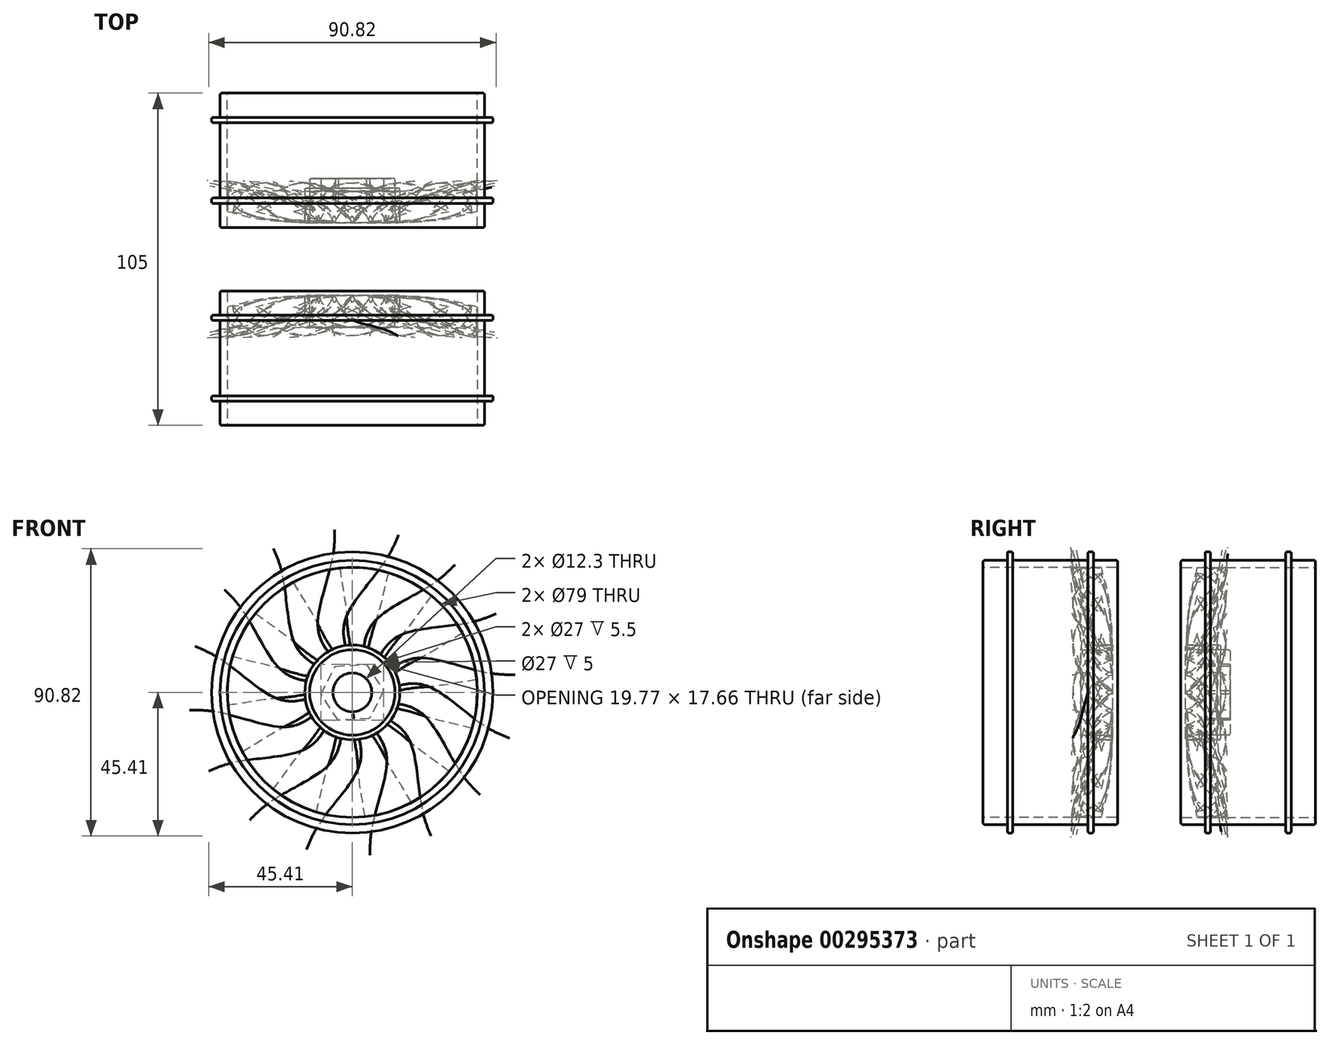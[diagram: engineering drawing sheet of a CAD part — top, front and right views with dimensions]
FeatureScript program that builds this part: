
annotation { "Feature Type Name" : "Feature", "Feature Type Description" : "" }
export const myFeature = defineFeature(function(context is Context, id is Id, definition is map)
    precondition{}
    {
        {
            var Q0;
            Q0=qCreatedBy(makeId("Front.planeOp"),FACE);
            var sketch = newSketch(context, id + "F0", { "sketchPlane" : qUnion([Q0])});
            skCircle(sketch, "E0", {"center": v(0, 0) * mm, "radius": 41.75 * mm});
            skCircle(sketch, "E1", {"center": v(0, 0) * mm, "radius": 55 * mm, "construction": true});
            skCircle(sketch, "E2", {"center": v(0, 0) * mm, "radius": 6.15 * mm});
            skCircle(sketch, "E3", {"center": v(0, 0) * mm, "radius": 39.5 * mm});
            skCircle(sketch, "E4", {"center": v(0, 0) * mm, "radius": 13.5 * mm});
            skCircle(sketch, "E5", {"center": v(0, 0) * mm, "radius": 15 * mm});
            skCircle(sketch, "E6.cCircle", {"center": v(0, 0) * mm, "radius": 9.9 * mm, "construction": true});
            skLineSegment(sketch, "E6.0", {"start": v(9.89, 0.54) * mm, "end": v(5.41, -8.3) * mm});
            skLineSegment(sketch, "E6.1", {"start": v(5.41, -8.3) * mm, "end": v(-4.47, -8.83) * mm});
            skLineSegment(sketch, "E6.2", {"start": v(-4.47, -8.83) * mm, "end": v(-9.89, -0.54) * mm});
            skLineSegment(sketch, "E6.3", {"start": v(-9.89, -0.54) * mm, "end": v(-5.41, 8.3) * mm});
            skLineSegment(sketch, "E6.4", {"start": v(-5.41, 8.3) * mm, "end": v(4.47, 8.83) * mm});
            skLineSegment(sketch, "E6.5", {"start": v(4.47, 8.83) * mm, "end": v(9.89, 0.54) * mm});
            skSolve(sketch);
        }
        {
            var Q0;
            Q0=makeQuery(id+"F0.imprint","IMPRINT",FACE,{"disambiguationData":[TD([[makeQuery(id+"F0.imprint","IMPRINT",EDGE,{"derivedFrom":sQuery(id+"F0.wireOp",EDGE,"E0")}),1.0]])]});
            extrude(context, id + "F1", {"entities" : qUnion([Q0]), "depth" : 3.5 * mm, "hasSecondDirection" : true, "secondDirectionOppositeDirection" : true, "secondDirectionDepth" : 39 * mm});
        }
        {
            var Q0;
            Q0=makeQuery(id+"F1.opExtrude","CAP_EDGE",EDGE,{"disambiguationData":[OSD([sQuery(id+"F0.wireOp",EDGE,"E3")])],"isStart":false});
            var Q1;
            Q1=makeQuery(id+"F1.opExtrude","CAP_EDGE",EDGE,{"disambiguationData":[OSD([sQuery(id+"F0.wireOp",EDGE,"E0")])],"isStart":false});
            var Q2;
            Q2=makeQuery(id+"F1.opExtrude","CAP_EDGE",EDGE,{"disambiguationData":[OSD([sQuery(id+"F0.wireOp",EDGE,"E3")])],"isStart":true});
            var Q3;
            Q3=makeQuery(id+"F1.opExtrude","CAP_EDGE",EDGE,{"disambiguationData":[OSD([sQuery(id+"F0.wireOp",EDGE,"E0")])],"isStart":true});
            fillet(context, id + "F2", {"entities" : qUnion([Q0, Q1, Q2, Q3]), "radius" : .5 * mm, "tangentPropagation" : true, "allowEdgeOverflow" : false});
        }
        {
            var Q0;
            Q0=makeQuery(id+"F0.imprint","IMPRINT",FACE,{"disambiguationData":[TD([[makeQuery(id+"F0.imprint","IMPRINT",EDGE,{"derivedFrom":sQuery(id+"F0.wireOp",EDGE,"E4")}),-1.0]])]});
            extrude(context, id + "F3", {"entities" : qUnion([Q0]), "oppositeDirection" : true, "depth" : 4 * mm, "hasSecondDirection" : true, "secondDirectionOppositeDirection" : false, "secondDirectionDepth" : 2 * mm, "offsetDistance" : 25 * mm});
        }
        {
            var Q0;
            Q0=makeQuery(id+"F0.imprint","IMPRINT",FACE,{"disambiguationData":[TD([[makeQuery(id+"F0.imprint","IMPRINT",EDGE,{"derivedFrom":sQuery(id+"F0.wireOp",EDGE,"E4")}),1.0]])]});
            var Q1;
            Q1=makeQuery(id+"F0.imprint","IMPRINT",FACE,{"disambiguationData":[TD([[makeQuery(id+"F0.imprint","IMPRINT",EDGE,{"derivedFrom":sQuery(id+"F0.wireOp",EDGE,"E2")}),-1.0]])]});
            extrude(context, id + "F4", {"entities" : qUnion([Q0, Q1]), "operationType" : NewBodyOperationType.ADD, "oppositeDirection" : true, "depth" : 8 * mm, "offsetDistance" : 25 * mm});
        }
        {
            var Q0;
            Q0=qCreatedBy(makeId("Top.planeOp"),FACE);
            cPlane(context, id + "F5", {"entities" : qUnion([Q0]), "cplaneType" : CPlaneType.OFFSET, "offset" : 12 * mm, "width" : 150 * mm, "height" : 150 * mm});
        }
        {
            var Q0;
            Q0=qCreatedBy(id+"F5.planeOp",FACE);
            var sketch = newSketch(context, id + "F6", { "sketchPlane" : qUnion([Q0])});
            skFitSpline(sketch, "E7", {"points": [v(0.53, -1.24) * mm, v(0.2, -1.6) * mm, v(-0.52, -1.05) * mm, v(-0.35, 1.79) * mm, v(0.58, 3.7) * mm, v(-0.1, -0.17) * mm, v(0.53, -1.24) * mm]});
            skSolve(sketch);
        }
        {
            var Q0;
            Q0=qCreatedBy(makeId("Top.planeOp"),FACE);
            cPlane(context, id + "F7", {"entities" : qUnion([Q0]), "cplaneType" : CPlaneType.OFFSET, "offset" : 40 * mm, "width" : 150 * mm, "height" : 150 * mm});
        }
        {
            var Q0;
            Q0=qCreatedBy(id+"F7.planeOp",FACE);
            var sketch = newSketch(context, id + "F8", { "sketchPlane" : qUnion([Q0])});
            skFitSpline(sketch, "E8", {"points": [v(-2.34, 1.57) * mm, v(-4.55, -0.94) * mm, v(-2.86, 4.8) * mm, v(9.88, 20.61) * mm, v(20.44, 27.72) * mm, v(5.15, 13.05) * mm, v(-2.34, 1.57) * mm]});
            skSolve(sketch);
        }
        {
            var Q0;
            Q0=qCreatedBy(id+"F5.planeOp",FACE);
            cPlane(context, id + "F9", {"entities" : qUnion([Q0]), "cplaneType" : CPlaneType.OFFSET, "offset" : 22 * mm, "width" : 150 * mm, "height" : 150 * mm});
        }
        {
            var Q0;
            Q0=qCreatedBy(id+"F9.planeOp",FACE);
            var sketch = newSketch(context, id + "F10", { "sketchPlane" : qUnion([Q0])});
            skPoint(sketch, "E9", {"position": v(-3.45, -1.13) * mm});
            skPoint(sketch, "E10", {"position": v(15.69, 22.06) * mm});
            skFitSpline(sketch, "E11", {"points": [v(-3.45, -1.13) * mm, v(-3.45, 2.76) * mm, v(4.28, 15.4) * mm, v(15.69, 22.06) * mm, v(4.3, 11.2) * mm, v(0, 0.78) * mm, v(-3.45, -1.13) * mm]});
            skSolve(sketch);
        }
        {
            var Q0;
            Q0=qCreatedBy(id+"F5.planeOp",FACE);
            cPlane(context, id + "F11", {"entities" : qUnion([Q0]), "cplaneType" : CPlaneType.OFFSET, "offset" : 10 * mm, "width" : 150 * mm, "height" : 150 * mm});
        }
        {
            var Q0;
            Q0=qCreatedBy(id+"F11.planeOp",FACE);
            var sketch = newSketch(context, id + "F12", { "sketchPlane" : qUnion([Q0])});
            skPoint(sketch, "E12", {"position": v(-1.84, -1.52) * mm});
            skFitSpline(sketch, "E13", {"points": [v(-1.84, -1.52) * mm, v(-1.84, 0.36) * mm, v(0.33, 5.91) * mm, v(2.1, 7.53) * mm, v(0.53, 2.14) * mm, v(-0.13, -1.72) * mm, v(-1.84, -1.52) * mm]});
            skSolve(sketch);
        }
        {
            var Q0;
            Q0=makeQuery(id+"F6.imprint","IMPRINT",FACE,{"disambiguationData":[TD([[makeQuery(id+"F6.imprint","IMPRINT",EDGE,{"derivedFrom":sQuery(id+"F6.wireOp",EDGE,"E7")}),-1.0]])]});
            var Q1;
            Q1=makeQuery(id+"F12.imprint","IMPRINT",FACE,{"disambiguationData":[TD([[makeQuery(id+"F12.imprint","IMPRINT",EDGE,{"derivedFrom":sQuery(id+"F12.wireOp",EDGE,"E13")}),-1.0]])]});
            var Q2;
            Q2=makeQuery(id+"F10.imprint","IMPRINT",FACE,{"disambiguationData":[TD([[makeQuery(id+"F10.imprint","IMPRINT",EDGE,{"derivedFrom":sQuery(id+"F10.wireOp",EDGE,"E11")}),-1.0]])]});
            var Q3;
            Q3=makeQuery(id+"F8.imprint","IMPRINT",FACE,{"disambiguationData":[TD([[makeQuery(id+"F8.imprint","IMPRINT",EDGE,{"derivedFrom":sQuery(id+"F8.wireOp",EDGE,"E8")}),-1.0]])]});
            var Q4;
            Q4=sQuery(id+"F12.wireOp",VERTEX,"E12");
            var Q5;
            Q5=sQuery(id+"F6.wireOp",VERTEX,"E7.1.internal");
            var Q6;
            Q6=sQuery(id+"F10.wireOp",VERTEX,"E9");
            var Q7;
            Q7=sQuery(id+"F8.wireOp",VERTEX,"E8.1.internal");
            loft(context, id + "F13", {"sheetProfilesArray" : [{ "sheetProfileEntities" : qUnion([Q0]) }, { "sheetProfileEntities" : qUnion([Q1]) }, { "sheetProfileEntities" : qUnion([Q2]) }, { "sheetProfileEntities" : qUnion([Q3]) }], "connections" : [{ "connectionEntities" : qUnion([Q4, Q5, Q6, Q7]), "connectionEdgeQueries" : qUnion([]), "connectionEdgeParameters" : [] }]});
        }
        {
            var Q0;
            Q0=qCreatedBy(makeId("Right.planeOp"),FACE);
            var sketch = newSketch(context, id + "F14", { "sketchPlane" : qUnion([Q0])});
            skLineSegment(sketch, "E14", {"start": v(-1.68, 13.92) * mm, "end": v(0, 48.42) * mm});
            skSolve(sketch);
        }
        {
            var Q0;
            Q0=makeQuery(id+"F13.opLoft","SWEPT_BODY",BODY,{"disambiguationData":[OSD([makeQuery(id+"F6.imprint","IMPRINT",FACE,{"disambiguationData":[TD([[makeQuery(id+"F6.imprint","IMPRINT",EDGE,{"derivedFrom":sQuery(id+"F6.wireOp",EDGE,"E7")}),-1.0]])]}),makeQuery(id+"F8.imprint","IMPRINT",FACE,{"disambiguationData":[TD([[makeQuery(id+"F8.imprint","IMPRINT",EDGE,{"derivedFrom":sQuery(id+"F8.wireOp",EDGE,"E8")}),-1.0]])]}),sQuery(id+"F10.wireOp",EDGE,"E11"),sQuery(id+"F12.wireOp",EDGE,"E13")])]});
            var Q1;
            Q1=sQuery(id+"F14.wireOp",EDGE,"E14");
            transform(context, id + "F15", {"entities" : qUnion([Q0]), "transformType" : TransformType.ROTATION, "transformAxis" : qUnion([Q1]), "angle" : 35 * degree, "oppositeDirection" : true, "makeCopy" : false});
        }
        {
            var Q0;
            Q0=makeQuery(id+"F1.opExtrude","SWEPT_BODY",BODY,{"disambiguationData":[OSD([sQuery(id+"F0.wireOp",EDGE,"E0"),sQuery(id+"F0.wireOp",EDGE,"E3")])]});
            var Q1;
            Q1=makeQuery(id+"F13.opLoft","SWEPT_BODY",BODY,{"disambiguationData":[OSD([makeQuery(id+"F6.imprint","IMPRINT",FACE,{"disambiguationData":[TD([[makeQuery(id+"F6.imprint","IMPRINT",EDGE,{"derivedFrom":sQuery(id+"F6.wireOp",EDGE,"E7")}),-1.0]])]}),makeQuery(id+"F8.imprint","IMPRINT",FACE,{"disambiguationData":[TD([[makeQuery(id+"F8.imprint","IMPRINT",EDGE,{"derivedFrom":sQuery(id+"F8.wireOp",EDGE,"E8")}),-1.0]])]}),sQuery(id+"F10.wireOp",EDGE,"E11"),sQuery(id+"F12.wireOp",EDGE,"E13")])]});
            var Q2;
            Q2=makeQuery(id+"F1.opExtrude","SWEPT_FACE",FACE,{"disambiguationData":[OSD([sQuery(id+"F0.wireOp",EDGE,"E0")])]});
            booleanBodies(context, id + "F16", {"operationType" : BooleanOperationType.SUBTRACTION, "tools" : qUnion([Q0]), "targets" : qUnion([Q1]), "offset" : true, "entitiesToOffset" : qUnion([Q2]), "offsetDistance" : 15 * mm, "keepTools" : true});
        }
        {
            var Q0;
            Q0=makeQuery(id+"F21.boolean.opBoolean","SPLIT",BODY,{"disambiguationData":[OD(0.0)],"derivedFrom":makeQuery(id+"F3.opExtrude","SWEPT_BODY",BODY,{"disambiguationData":[OSD([sQuery(id+"F0.wireOp",EDGE,"E4"),sQuery(id+"F0.wireOp",EDGE,"E5")])]})});
            var Q1;
            Q1=makeQuery(id+"F13.opLoft","SWEPT_BODY",BODY,{"disambiguationData":[OSD([makeQuery(id+"F6.imprint","IMPRINT",FACE,{"disambiguationData":[TD([[makeQuery(id+"F6.imprint","IMPRINT",EDGE,{"derivedFrom":sQuery(id+"F6.wireOp",EDGE,"E7")}),-1.0]])]}),makeQuery(id+"F8.imprint","IMPRINT",FACE,{"disambiguationData":[TD([[makeQuery(id+"F8.imprint","IMPRINT",EDGE,{"derivedFrom":sQuery(id+"F8.wireOp",EDGE,"E8")}),-1.0]])]}),sQuery(id+"F10.wireOp",EDGE,"E11"),sQuery(id+"F12.wireOp",EDGE,"E13")])]});
            var Q2;
            {var subQ0=sQuery(id+"F0.wireOp",EDGE,"E4");Q2=makeQuery(id+"F21.boolean.opBoolean","MERGE",FACE,{"derivedFrom":[makeQuery(id+"F3.opExtrude","SWEPT_FACE",FACE,{"disambiguationData":[OSD([subQ0])]}),makeQuery(id+"F21.opExtrude","SWEPT_FACE",FACE,{"disambiguationData":[OSD([subQ0])]})]});}
            var Q3;
            {var subQ0=sQuery(id+"F0.wireOp",EDGE,"E4");Q3=makeQuery(id+"F29.opFillet","BLEND_FACE",FACE,{"disambiguationData":[OSD([subQ0]),TDD([makeQuery(id+"F3.opExtrude","CAP_EDGE",EDGE,{"disambiguationData":[OSD([subQ0])],"isStart":true})])]});}
            booleanBodies(context, id + "F17", {"operationType" : BooleanOperationType.SUBTRACTION, "tools" : qUnion([Q0]), "targets" : qUnion([Q1]), "offset" : true, "entitiesToOffset" : qUnion([Q2, Q3]), "offsetDistance" : 5 * mm, "keepTools" : true});
        }
        {
            var Q0;
            Q0=makeQuery(id+"F13.opLoft","SWEPT_BODY",BODY,{"disambiguationData":[OSD([makeQuery(id+"F6.imprint","IMPRINT",FACE,{"disambiguationData":[TD([[makeQuery(id+"F6.imprint","IMPRINT",EDGE,{"derivedFrom":sQuery(id+"F6.wireOp",EDGE,"E7")}),-1.0]])]}),makeQuery(id+"F8.imprint","IMPRINT",FACE,{"disambiguationData":[TD([[makeQuery(id+"F8.imprint","IMPRINT",EDGE,{"derivedFrom":sQuery(id+"F8.wireOp",EDGE,"E8")}),-1.0]])]}),sQuery(id+"F10.wireOp",EDGE,"E11"),sQuery(id+"F12.wireOp",EDGE,"E13")])]});
            var Q1;
            Q1=makeQuery(id+"F4.opExtrude","SWEPT_FACE",FACE,{"disambiguationData":[OSD([sQuery(id+"F0.wireOp",EDGE,"E2")])]});
            circularPattern(context, id + "F18", {"entities" : qUnion([Q0]), "axis" : qUnion([Q1]), "angle" : 360 * degree, "instanceCount" : 16, "equalSpace" : true});
        }
        {
            var Q0;
            {var subQ0=sQuery(id+"F0.wireOp",EDGE,"E4");Q0=makeQuery(id+"F4.boolean.opBoolean","MERGE",FACE,{"derivedFrom":[makeQuery(id+"F3.opExtrude","CAP_FACE",FACE,{"disambiguationData":[OSD([subQ0,sQuery(id+"F0.wireOp",EDGE,"E5")])],"isStart":false}),makeQuery(id+"F4.opExtrude","CAP_FACE",FACE,{"disambiguationData":[OSD([sQuery(id+"F0.wireOp",EDGE,"E2"),subQ0])],"isStart":false})]});}
            var sketch = newSketch(context, id + "F19", { "sketchPlane" : qUnion([Q0])});
            skLineSegment(sketch, "E15.0", {"start": v(9.89, -0.54) * mm, "end": v(5.41, 8.3) * mm});
            skLineSegment(sketch, "E15.1", {"start": v(5.41, 8.3) * mm, "end": v(-4.47, 8.83) * mm});
            skLineSegment(sketch, "E15.2", {"start": v(-4.47, 8.83) * mm, "end": v(-9.89, 0.54) * mm});
            skLineSegment(sketch, "E15.3", {"start": v(-9.89, 0.54) * mm, "end": v(-5.41, -8.3) * mm});
            skLineSegment(sketch, "E15.4", {"start": v(-5.41, -8.3) * mm, "end": v(4.47, -8.83) * mm});
            skLineSegment(sketch, "E15.5", {"start": v(4.47, -8.83) * mm, "end": v(9.89, -0.54) * mm});
            skSolve(sketch);
        }
        {
            var Q0;
            Q0=makeQuery(id+"F19.imprint","IMPRINT",FACE,{"disambiguationData":[TD([[makeQuery(id+"F19.imprint","IMPRINT",EDGE,{"derivedFrom":sQuery(id+"F19.wireOp",EDGE,"E15.0")}),-1.0]])]});
            extrude(context, id + "F20", {"entities" : qUnion([Q0]), "depth" : 8 * mm, "offsetDistance" : 25 * mm});
        }
        {
            var Q0;
            Q0=makeQuery(id+"F4.opExtrude","CAP_FACE",FACE,{"disambiguationData":[OSD([sQuery(id+"F0.wireOp",EDGE,"E2"),sQuery(id+"F0.wireOp",EDGE,"E4")])],"isStart":true});
            extrude(context, id + "F21", {"entities" : qUnion([Q0]), "operationType" : NewBodyOperationType.REMOVE, "oppositeDirection" : true, "depth" : 4 * mm, "offsetDistance" : 25 * mm});
        }
        {
            var Q0;
            Q0=makeQuery(id+"F1.opExtrude","CAP_FACE",FACE,{"disambiguationData":[OSD([sQuery(id+"F0.wireOp",EDGE,"E0"),sQuery(id+"F0.wireOp",EDGE,"E3")])],"isStart":false});
            cPlane(context, id + "F22", {"entities" : qUnion([Q0]), "cplaneType" : CPlaneType.OFFSET, "offset" : 8.5 * mm, "oppositeDirection" : true, "width" : 150 * mm, "height" : 150 * mm});
        }
        {
            var Q0;
            Q0=qCreatedBy(id+"F22.planeOp",FACE);
            var sketch = newSketch(context, id + "F23", { "sketchPlane" : qUnion([Q0])});
            skCircle(sketch, "E16", {"center": v(0, 0) * mm, "radius": 44.45 * mm});
            skCircle(sketch, "E17", {"center": v(0, 0) * mm, "radius": 41.75 * mm});
            skSolve(sketch);
        }
        {
            var Q0;
            Q0=makeQuery(id+"F23.imprint","IMPRINT",FACE,{"disambiguationData":[TD([[makeQuery(id+"F23.imprint","IMPRINT",EDGE,{"derivedFrom":sQuery(id+"F23.wireOp",EDGE,"E16")}),1.0]])]});
            extrude(context, id + "F24", {"entities" : qUnion([Q0]), "operationType" : NewBodyOperationType.ADD, "depth" : 1.7 * mm, "offsetDistance" : 25 * mm, "symmetric" : true});
        }
        {
            var Q0;
            Q0=makeQuery(id+"F1.opExtrude","CAP_FACE",FACE,{"disambiguationData":[OSD([sQuery(id+"F0.wireOp",EDGE,"E0"),sQuery(id+"F0.wireOp",EDGE,"E3")])],"isStart":false});
            cPlane(context, id + "F25", {"entities" : qUnion([Q0]), "cplaneType" : CPlaneType.OFFSET, "offset" : 34 * mm, "oppositeDirection" : true, "width" : 150 * mm, "height" : 150 * mm});
        }
        {
            var Q0;
            Q0=qCreatedBy(id+"F25.planeOp",FACE);
            var sketch = newSketch(context, id + "F26", { "sketchPlane" : qUnion([Q0])});
            skCircle(sketch, "E18.0", {"center": v(0, 0) * mm, "radius": 41.75 * mm});
            skCircle(sketch, "E19.0", {"center": v(0, 0) * mm, "radius": 44.45 * mm});
            skSolve(sketch);
        }
        {
            var Q0;
            Q0=makeQuery(id+"F26.imprint","IMPRINT",FACE,{"disambiguationData":[TD([[makeQuery(id+"F26.imprint","IMPRINT",EDGE,{"derivedFrom":sQuery(id+"F26.wireOp",EDGE,"E18.0")}),-1.0]])]});
            extrude(context, id + "F27", {"entities" : qUnion([Q0]), "operationType" : NewBodyOperationType.ADD, "depth" : 1.7 * mm, "offsetDistance" : 25 * mm, "symmetric" : true});
        }
        {
            var Q0;
            Q0=makeQuery(id+"F19.imprint","IMPRINT",FACE,{"disambiguationData":[TD([[makeQuery(id+"F19.imprint","IMPRINT",EDGE,{"derivedFrom":makeQuery(id+"F3.opExtrude","CAP_EDGE",EDGE,{"disambiguationData":[OSD([sQuery(id+"F0.wireOp",EDGE,"E5")])],"isStart":false})}),-1.0]])]});
            extrude(context, id + "F28", {"entities" : qUnion([Q0]), "depth" : 5 * mm, "offsetDistance" : 25 * mm});
        }
        {
            var Q0;
            Q0=makeQuery(id+"F20.opExtrude","CAP_EDGE",EDGE,{"disambiguationData":[OSD([sQuery(id+"F0.wireOp",EDGE,"E4")])],"isStart":true});
            var Q1;
            Q1=makeQuery(id+"F3.opExtrude","CAP_EDGE",EDGE,{"disambiguationData":[OSD([sQuery(id+"F0.wireOp",EDGE,"E4")])],"isStart":true});
            var Q2;
            Q2=makeQuery(id+"F3.opExtrude","CAP_EDGE",EDGE,{"disambiguationData":[OSD([sQuery(id+"F0.wireOp",EDGE,"E5")])],"isStart":true});
            var Q3;
            Q3=makeQuery(id+"F24.opExtrude","CAP_EDGE",EDGE,{"disambiguationData":[OSD([sQuery(id+"F23.wireOp",EDGE,"E16")])],"isStart":false});
            var Q4;
            Q4=makeQuery(id+"F24.opExtrude","CAP_EDGE",EDGE,{"disambiguationData":[OSD([sQuery(id+"F23.wireOp",EDGE,"E16")])],"isStart":true});
            var Q5;
            Q5=makeQuery(id+"F27.opExtrude","CAP_EDGE",EDGE,{"disambiguationData":[OSD([sQuery(id+"F26.wireOp",EDGE,"E19.0")])],"isStart":false});
            var Q6;
            Q6=makeQuery(id+"F27.opExtrude","CAP_EDGE",EDGE,{"disambiguationData":[OSD([sQuery(id+"F26.wireOp",EDGE,"E19.0")])],"isStart":true});
            var Q7;
            Q7=makeQuery(id+"F20.opExtrude","CAP_EDGE",EDGE,{"disambiguationData":[OSD([sQuery(id+"F0.wireOp",EDGE,"E4")])],"isStart":false});
            var Q8;
            Q8=makeQuery(id+"F28.opExtrude","CAP_EDGE",EDGE,{"disambiguationData":[OSD([sQuery(id+"F0.wireOp",EDGE,"E5")])],"isStart":false});
            fillet(context, id + "F29", {"entities" : qUnion([Q0, Q1, Q2, Q3, Q4, Q5, Q6, Q7, Q8]), "radius" : 0.5 * mm, "tangentPropagation" : true, "allowEdgeOverflow" : false});
        }
        {
            var Q0;
            Q0=makeQuery(id+"F1.opExtrude","CAP_FACE",FACE,{"disambiguationData":[OSD([sQuery(id+"F0.wireOp",EDGE,"E0"),sQuery(id+"F0.wireOp",EDGE,"E3")])],"isStart":false});
            cPlane(context, id + "F30", {"entities" : qUnion([Q0]), "cplaneType" : CPlaneType.OFFSET, "offset" : 10 * mm, "width" : 150 * mm, "height" : 150 * mm});
        }
        {
            var Q0;
            Q0=makeQuery(id+"F1.opExtrude","SWEPT_BODY",BODY,{"disambiguationData":[OSD([sQuery(id+"F0.wireOp",EDGE,"E0"),sQuery(id+"F0.wireOp",EDGE,"E3")])]});
            var Q1;
            Q1=makeQuery(id+"F13.opLoft","SWEPT_BODY",BODY,{"disambiguationData":[OSD([makeQuery(id+"F6.imprint","IMPRINT",FACE,{"disambiguationData":[TD([[makeQuery(id+"F6.imprint","IMPRINT",EDGE,{"derivedFrom":sQuery(id+"F6.wireOp",EDGE,"E7")}),-1.0]])]}),makeQuery(id+"F8.imprint","IMPRINT",FACE,{"disambiguationData":[TD([[makeQuery(id+"F8.imprint","IMPRINT",EDGE,{"derivedFrom":sQuery(id+"F8.wireOp",EDGE,"E8")}),-1.0]])]}),sQuery(id+"F10.wireOp",EDGE,"E11"),sQuery(id+"F12.wireOp",EDGE,"E13")])]});
            var Q2;
            Q2=makeQuery(id+"F18.opPattern","COPY",BODY,{"derivedFrom":makeQuery(id+"F13.opLoft","SWEPT_BODY",BODY,{"disambiguationData":[OSD([makeQuery(id+"F6.imprint","IMPRINT",FACE,{"disambiguationData":[TD([[makeQuery(id+"F6.imprint","IMPRINT",EDGE,{"derivedFrom":sQuery(id+"F6.wireOp",EDGE,"E7")}),-1.0]])]}),makeQuery(id+"F8.imprint","IMPRINT",FACE,{"disambiguationData":[TD([[makeQuery(id+"F8.imprint","IMPRINT",EDGE,{"derivedFrom":sQuery(id+"F8.wireOp",EDGE,"E8")}),-1.0]])]}),sQuery(id+"F10.wireOp",EDGE,"E11"),sQuery(id+"F12.wireOp",EDGE,"E13")])]}),"instanceName":"1"});
            var Q3;
            Q3=makeQuery(id+"F18.opPattern","COPY",BODY,{"derivedFrom":makeQuery(id+"F13.opLoft","SWEPT_BODY",BODY,{"disambiguationData":[OSD([makeQuery(id+"F6.imprint","IMPRINT",FACE,{"disambiguationData":[TD([[makeQuery(id+"F6.imprint","IMPRINT",EDGE,{"derivedFrom":sQuery(id+"F6.wireOp",EDGE,"E7")}),-1.0]])]}),makeQuery(id+"F8.imprint","IMPRINT",FACE,{"disambiguationData":[TD([[makeQuery(id+"F8.imprint","IMPRINT",EDGE,{"derivedFrom":sQuery(id+"F8.wireOp",EDGE,"E8")}),-1.0]])]}),sQuery(id+"F10.wireOp",EDGE,"E11"),sQuery(id+"F12.wireOp",EDGE,"E13")])]}),"instanceName":"4"});
            var Q4;
            Q4=makeQuery(id+"F18.opPattern","COPY",BODY,{"derivedFrom":makeQuery(id+"F13.opLoft","SWEPT_BODY",BODY,{"disambiguationData":[OSD([makeQuery(id+"F6.imprint","IMPRINT",FACE,{"disambiguationData":[TD([[makeQuery(id+"F6.imprint","IMPRINT",EDGE,{"derivedFrom":sQuery(id+"F6.wireOp",EDGE,"E7")}),-1.0]])]}),makeQuery(id+"F8.imprint","IMPRINT",FACE,{"disambiguationData":[TD([[makeQuery(id+"F8.imprint","IMPRINT",EDGE,{"derivedFrom":sQuery(id+"F8.wireOp",EDGE,"E8")}),-1.0]])]}),sQuery(id+"F10.wireOp",EDGE,"E11"),sQuery(id+"F12.wireOp",EDGE,"E13")])]}),"instanceName":"5"});
            var Q5;
            Q5=makeQuery(id+"F18.opPattern","COPY",BODY,{"derivedFrom":makeQuery(id+"F13.opLoft","SWEPT_BODY",BODY,{"disambiguationData":[OSD([makeQuery(id+"F6.imprint","IMPRINT",FACE,{"disambiguationData":[TD([[makeQuery(id+"F6.imprint","IMPRINT",EDGE,{"derivedFrom":sQuery(id+"F6.wireOp",EDGE,"E7")}),-1.0]])]}),makeQuery(id+"F8.imprint","IMPRINT",FACE,{"disambiguationData":[TD([[makeQuery(id+"F8.imprint","IMPRINT",EDGE,{"derivedFrom":sQuery(id+"F8.wireOp",EDGE,"E8")}),-1.0]])]}),sQuery(id+"F10.wireOp",EDGE,"E11"),sQuery(id+"F12.wireOp",EDGE,"E13")])]}),"instanceName":"6"});
            var Q6;
            Q6=makeQuery(id+"F18.opPattern","COPY",BODY,{"derivedFrom":makeQuery(id+"F13.opLoft","SWEPT_BODY",BODY,{"disambiguationData":[OSD([makeQuery(id+"F6.imprint","IMPRINT",FACE,{"disambiguationData":[TD([[makeQuery(id+"F6.imprint","IMPRINT",EDGE,{"derivedFrom":sQuery(id+"F6.wireOp",EDGE,"E7")}),-1.0]])]}),makeQuery(id+"F8.imprint","IMPRINT",FACE,{"disambiguationData":[TD([[makeQuery(id+"F8.imprint","IMPRINT",EDGE,{"derivedFrom":sQuery(id+"F8.wireOp",EDGE,"E8")}),-1.0]])]}),sQuery(id+"F10.wireOp",EDGE,"E11"),sQuery(id+"F12.wireOp",EDGE,"E13")])]}),"instanceName":"7"});
            var Q7;
            Q7=makeQuery(id+"F18.opPattern","COPY",BODY,{"derivedFrom":makeQuery(id+"F13.opLoft","SWEPT_BODY",BODY,{"disambiguationData":[OSD([makeQuery(id+"F6.imprint","IMPRINT",FACE,{"disambiguationData":[TD([[makeQuery(id+"F6.imprint","IMPRINT",EDGE,{"derivedFrom":sQuery(id+"F6.wireOp",EDGE,"E7")}),-1.0]])]}),makeQuery(id+"F8.imprint","IMPRINT",FACE,{"disambiguationData":[TD([[makeQuery(id+"F8.imprint","IMPRINT",EDGE,{"derivedFrom":sQuery(id+"F8.wireOp",EDGE,"E8")}),-1.0]])]}),sQuery(id+"F10.wireOp",EDGE,"E11"),sQuery(id+"F12.wireOp",EDGE,"E13")])]}),"instanceName":"8"});
            var Q8;
            Q8=makeQuery(id+"F18.opPattern","COPY",BODY,{"derivedFrom":makeQuery(id+"F13.opLoft","SWEPT_BODY",BODY,{"disambiguationData":[OSD([makeQuery(id+"F6.imprint","IMPRINT",FACE,{"disambiguationData":[TD([[makeQuery(id+"F6.imprint","IMPRINT",EDGE,{"derivedFrom":sQuery(id+"F6.wireOp",EDGE,"E7")}),-1.0]])]}),makeQuery(id+"F8.imprint","IMPRINT",FACE,{"disambiguationData":[TD([[makeQuery(id+"F8.imprint","IMPRINT",EDGE,{"derivedFrom":sQuery(id+"F8.wireOp",EDGE,"E8")}),-1.0]])]}),sQuery(id+"F10.wireOp",EDGE,"E11"),sQuery(id+"F12.wireOp",EDGE,"E13")])]}),"instanceName":"9"});
            var Q9;
            Q9=makeQuery(id+"F18.opPattern","COPY",BODY,{"derivedFrom":makeQuery(id+"F13.opLoft","SWEPT_BODY",BODY,{"disambiguationData":[OSD([makeQuery(id+"F6.imprint","IMPRINT",FACE,{"disambiguationData":[TD([[makeQuery(id+"F6.imprint","IMPRINT",EDGE,{"derivedFrom":sQuery(id+"F6.wireOp",EDGE,"E7")}),-1.0]])]}),makeQuery(id+"F8.imprint","IMPRINT",FACE,{"disambiguationData":[TD([[makeQuery(id+"F8.imprint","IMPRINT",EDGE,{"derivedFrom":sQuery(id+"F8.wireOp",EDGE,"E8")}),-1.0]])]}),sQuery(id+"F10.wireOp",EDGE,"E11"),sQuery(id+"F12.wireOp",EDGE,"E13")])]}),"instanceName":"10"});
            var Q10;
            Q10=makeQuery(id+"F18.opPattern","COPY",BODY,{"derivedFrom":makeQuery(id+"F13.opLoft","SWEPT_BODY",BODY,{"disambiguationData":[OSD([makeQuery(id+"F6.imprint","IMPRINT",FACE,{"disambiguationData":[TD([[makeQuery(id+"F6.imprint","IMPRINT",EDGE,{"derivedFrom":sQuery(id+"F6.wireOp",EDGE,"E7")}),-1.0]])]}),makeQuery(id+"F8.imprint","IMPRINT",FACE,{"disambiguationData":[TD([[makeQuery(id+"F8.imprint","IMPRINT",EDGE,{"derivedFrom":sQuery(id+"F8.wireOp",EDGE,"E8")}),-1.0]])]}),sQuery(id+"F10.wireOp",EDGE,"E11"),sQuery(id+"F12.wireOp",EDGE,"E13")])]}),"instanceName":"11"});
            var Q11;
            Q11=makeQuery(id+"F18.opPattern","COPY",BODY,{"derivedFrom":makeQuery(id+"F13.opLoft","SWEPT_BODY",BODY,{"disambiguationData":[OSD([makeQuery(id+"F6.imprint","IMPRINT",FACE,{"disambiguationData":[TD([[makeQuery(id+"F6.imprint","IMPRINT",EDGE,{"derivedFrom":sQuery(id+"F6.wireOp",EDGE,"E7")}),-1.0]])]}),makeQuery(id+"F8.imprint","IMPRINT",FACE,{"disambiguationData":[TD([[makeQuery(id+"F8.imprint","IMPRINT",EDGE,{"derivedFrom":sQuery(id+"F8.wireOp",EDGE,"E8")}),-1.0]])]}),sQuery(id+"F10.wireOp",EDGE,"E11"),sQuery(id+"F12.wireOp",EDGE,"E13")])]}),"instanceName":"12"});
            var Q12;
            Q12=makeQuery(id+"F18.opPattern","COPY",BODY,{"derivedFrom":makeQuery(id+"F13.opLoft","SWEPT_BODY",BODY,{"disambiguationData":[OSD([makeQuery(id+"F6.imprint","IMPRINT",FACE,{"disambiguationData":[TD([[makeQuery(id+"F6.imprint","IMPRINT",EDGE,{"derivedFrom":sQuery(id+"F6.wireOp",EDGE,"E7")}),-1.0]])]}),makeQuery(id+"F8.imprint","IMPRINT",FACE,{"disambiguationData":[TD([[makeQuery(id+"F8.imprint","IMPRINT",EDGE,{"derivedFrom":sQuery(id+"F8.wireOp",EDGE,"E8")}),-1.0]])]}),sQuery(id+"F10.wireOp",EDGE,"E11"),sQuery(id+"F12.wireOp",EDGE,"E13")])]}),"instanceName":"13"});
            var Q13;
            Q13=makeQuery(id+"F18.opPattern","COPY",BODY,{"derivedFrom":makeQuery(id+"F13.opLoft","SWEPT_BODY",BODY,{"disambiguationData":[OSD([makeQuery(id+"F6.imprint","IMPRINT",FACE,{"disambiguationData":[TD([[makeQuery(id+"F6.imprint","IMPRINT",EDGE,{"derivedFrom":sQuery(id+"F6.wireOp",EDGE,"E7")}),-1.0]])]}),makeQuery(id+"F8.imprint","IMPRINT",FACE,{"disambiguationData":[TD([[makeQuery(id+"F8.imprint","IMPRINT",EDGE,{"derivedFrom":sQuery(id+"F8.wireOp",EDGE,"E8")}),-1.0]])]}),sQuery(id+"F10.wireOp",EDGE,"E11"),sQuery(id+"F12.wireOp",EDGE,"E13")])]}),"instanceName":"14"});
            var Q14;
            Q14=makeQuery(id+"F18.opPattern","COPY",BODY,{"derivedFrom":makeQuery(id+"F13.opLoft","SWEPT_BODY",BODY,{"disambiguationData":[OSD([makeQuery(id+"F6.imprint","IMPRINT",FACE,{"disambiguationData":[TD([[makeQuery(id+"F6.imprint","IMPRINT",EDGE,{"derivedFrom":sQuery(id+"F6.wireOp",EDGE,"E7")}),-1.0]])]}),makeQuery(id+"F8.imprint","IMPRINT",FACE,{"disambiguationData":[TD([[makeQuery(id+"F8.imprint","IMPRINT",EDGE,{"derivedFrom":sQuery(id+"F8.wireOp",EDGE,"E8")}),-1.0]])]}),sQuery(id+"F10.wireOp",EDGE,"E11"),sQuery(id+"F12.wireOp",EDGE,"E13")])]}),"instanceName":"15"});
            var Q15;
            Q15=makeQuery(id+"F21.boolean.opBoolean","SPLIT",BODY,{"disambiguationData":[OD(0.0)],"derivedFrom":makeQuery(id+"F3.opExtrude","SWEPT_BODY",BODY,{"disambiguationData":[OSD([sQuery(id+"F0.wireOp",EDGE,"E4"),sQuery(id+"F0.wireOp",EDGE,"E5")])]})});
            var Q16;
            Q16=makeQuery(id+"F18.opPattern","COPY",BODY,{"derivedFrom":makeQuery(id+"F13.opLoft","SWEPT_BODY",BODY,{"disambiguationData":[OSD([makeQuery(id+"F6.imprint","IMPRINT",FACE,{"disambiguationData":[TD([[makeQuery(id+"F6.imprint","IMPRINT",EDGE,{"derivedFrom":sQuery(id+"F6.wireOp",EDGE,"E7")}),-1.0]])]}),makeQuery(id+"F8.imprint","IMPRINT",FACE,{"disambiguationData":[TD([[makeQuery(id+"F8.imprint","IMPRINT",EDGE,{"derivedFrom":sQuery(id+"F8.wireOp",EDGE,"E8")}),-1.0]])]}),sQuery(id+"F10.wireOp",EDGE,"E11"),sQuery(id+"F12.wireOp",EDGE,"E13")])]}),"instanceName":"2"});
            var Q17;
            Q17=makeQuery(id+"F18.opPattern","COPY",BODY,{"derivedFrom":makeQuery(id+"F13.opLoft","SWEPT_BODY",BODY,{"disambiguationData":[OSD([makeQuery(id+"F6.imprint","IMPRINT",FACE,{"disambiguationData":[TD([[makeQuery(id+"F6.imprint","IMPRINT",EDGE,{"derivedFrom":sQuery(id+"F6.wireOp",EDGE,"E7")}),-1.0]])]}),makeQuery(id+"F8.imprint","IMPRINT",FACE,{"disambiguationData":[TD([[makeQuery(id+"F8.imprint","IMPRINT",EDGE,{"derivedFrom":sQuery(id+"F8.wireOp",EDGE,"E8")}),-1.0]])]}),sQuery(id+"F10.wireOp",EDGE,"E11"),sQuery(id+"F12.wireOp",EDGE,"E13")])]}),"instanceName":"3"});
            var Q18;
            Q18=qCreatedBy(id+"F30.planeOp",FACE);
            mirror(context, id + "F31", {"entities" : qUnion([Q0, Q1, Q2, Q3, Q4, Q5, Q6, Q7, Q8, Q9, Q10, Q11, Q12, Q13, Q14, Q15, Q16, Q17]), "mirrorPlane" : qUnion([Q18])});
        }
        {
            var Q0;
            Q0=makeQuery(id+"F4.opExtrude","CAP_FACE",FACE,{"disambiguationData":[OSD([sQuery(id+"F0.wireOp",EDGE,"E2"),sQuery(id+"F0.wireOp",EDGE,"E4")])],"isStart":false});
            var sketch = newSketch(context, id + "F32", { "sketchPlane" : qUnion([Q0])});
            skText(sketch, "E20", { "text": "R", "fontName": "OpenSans-Regular.ttf"});
            const initialGuessF32  = {"E20": [-0.0009, -0.00802, 1, 0, 0.00106]};
            skSetInitialGuess(sketch, initialGuessF32);
            skSolve(sketch);
        }
        {
            var Q0;
            Q0=makeQuery(id+"F32.imprint","IMPRINT",FACE,{"disambiguationData":[TD([[makeQuery(id+"F32.imprint","IMPRINT",EDGE,{"derivedFrom":sQuery(id+"F32.wireOp",EDGE,"E20.sketch_text.stroke-0")}),-1.0]])]});
            extrude(context, id + "F33", {"entities" : qUnion([Q0]), "operationType" : NewBodyOperationType.REMOVE, "oppositeDirection" : true, "depth" : 0.1 * mm, "offsetDistance" : 25 * mm});
        }
        {
            var Q0;
            Q0=makeQuery(id+"F31.opPattern","COPY",FACE,{"derivedFrom":makeQuery(id+"F4.opExtrude","CAP_FACE",FACE,{"disambiguationData":[OSD([sQuery(id+"F0.wireOp",EDGE,"E2"),sQuery(id+"F0.wireOp",EDGE,"E4")])],"isStart":false}),"instanceName":"1"});
            var sketch = newSketch(context, id + "F34", { "sketchPlane" : qUnion([Q0])});
            skText(sketch, "E21", { "text": "L", "fontName": "OpenSans-Regular.ttf"});
            const initialGuessF34  = {"E21": [0, -0.00795, 1, 0, 0.00112]};
            skSetInitialGuess(sketch, initialGuessF34);
            skSolve(sketch);
        }
        {
            var Q0;
            Q0=makeQuery(id+"F34.imprint","IMPRINT",FACE,{"disambiguationData":[TD([[makeQuery(id+"F34.imprint","IMPRINT",EDGE,{"derivedFrom":sQuery(id+"F34.wireOp",EDGE,"E21.sketch_text.stroke-0")}),-1.0]])]});
            extrude(context, id + "F35", {"entities" : qUnion([Q0]), "operationType" : NewBodyOperationType.REMOVE, "oppositeDirection" : true, "depth" : 0.1 * mm, "offsetDistance" : 25 * mm});
        }
    });
